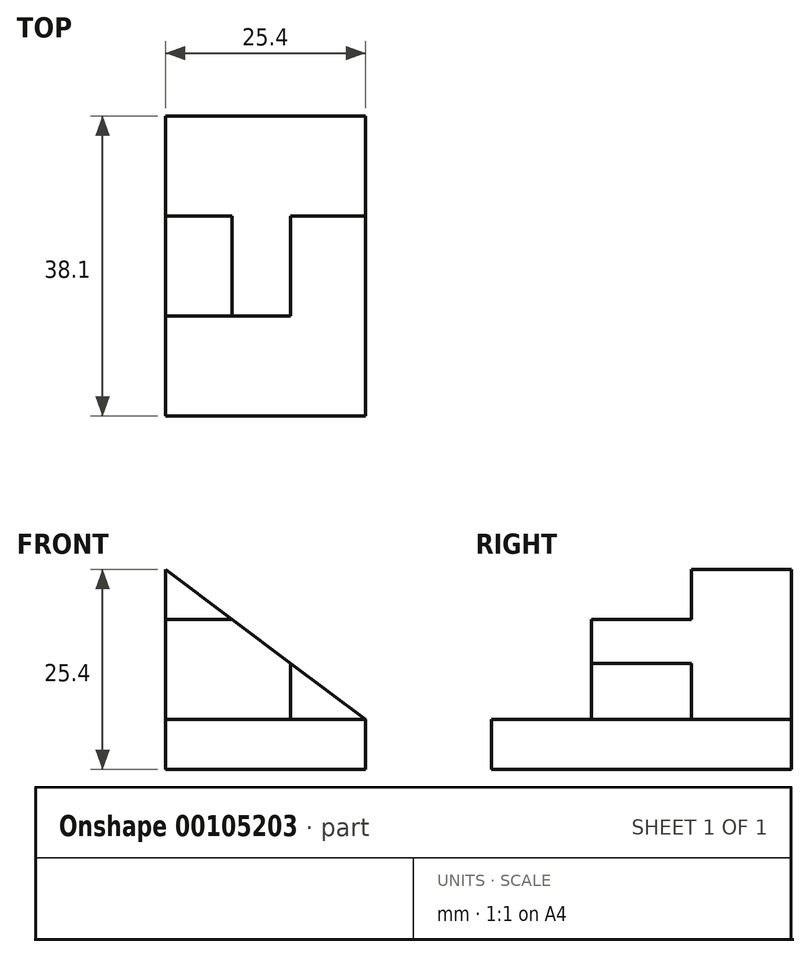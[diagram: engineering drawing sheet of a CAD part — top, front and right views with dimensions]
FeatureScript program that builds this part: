
annotation { "Feature Type Name" : "Feature", "Feature Type Description" : "" }
export const myFeature = defineFeature(function(context is Context, id is Id, definition is map)
    precondition{}
    {
        {
            var Q0;
            Q0=qCreatedBy(makeId("Front.planeOp"),FACE);
            var sketch = newSketch(context, id + "F0", { "sketchPlane" : qUnion([Q0])});
            skLineSegment(sketch, "E0.bottom", {"start": v(0, 0) * mm, "end": v(-25.4, 0) * mm});
            skLineSegment(sketch, "E0.left", {"start": v(0, 0) * mm, "end": v(0, 6.35) * mm});
            skLineSegment(sketch, "E0.right", {"start": v(-25.4, 0) * mm, "end": v(-25.4, 25.4) * mm});
            skLineSegment(sketch, "E1", {"start": v(-25.4, 25.4) * mm, "end": v(0, 6.35) * mm});
            skSolve(sketch);
        }
        {
            var Q0;
            Q0 = qSketchRegion(id + "F0", true);
            extrude(context, id + "F1", {"entities" : qUnion([Q0]), "oppositeDirection" : true, "depth" : 38.1 * mm});
        }
        {
            var Q0;
            Q0=qCreatedBy(makeId("Right.planeOp"),FACE);
            var sketch = newSketch(context, id + "F2", { "sketchPlane" : qUnion([Q0])});
            skLineSegment(sketch, "E2.bottom", {"start": v(12.7, 25.4) * mm, "end": v(0, 25.4) * mm});
            skLineSegment(sketch, "E2.top", {"start": v(12.7, 6.35) * mm, "end": v(0, 6.35) * mm});
            skLineSegment(sketch, "E2.left", {"start": v(12.7, 25.4) * mm, "end": v(12.7, 6.35) * mm});
            skLineSegment(sketch, "E2.right", {"start": v(0, 25.4) * mm, "end": v(0, 6.35) * mm});
            skSolve(sketch);
        }
        {
            var Q0;
            Q0 = qSketchRegion(id + "F2", true);
            extrude(context, id + "F3", {"entities" : qUnion([Q0]), "operationType" : NewBodyOperationType.REMOVE, "oppositeDirection" : true, "depth" : 25.4 * mm});
        }
        {
            var Q0;
            Q0=qCreatedBy(makeId("Right.planeOp"),FACE);
            var sketch = newSketch(context, id + "F4", { "sketchPlane" : qUnion([Q0])});
            skLineSegment(sketch, "E3.bottom", {"start": v(12.7, 25.4) * mm, "end": v(25.4, 25.4) * mm});
            skLineSegment(sketch, "E3.top", {"start": v(12.7, 19.05) * mm, "end": v(25.4, 19.05) * mm});
            skLineSegment(sketch, "E3.left", {"start": v(12.7, 25.4) * mm, "end": v(12.7, 19.05) * mm});
            skLineSegment(sketch, "E3.right", {"start": v(25.4, 25.4) * mm, "end": v(25.4, 19.05) * mm});
            skSolve(sketch);
        }
        {
            var Q0;
            Q0 = qSketchRegion(id + "F4", true);
            extrude(context, id + "F5", {"entities" : qUnion([Q0]), "operationType" : NewBodyOperationType.REMOVE, "oppositeDirection" : true, "depth" : 25.4 * mm});
        }
        {
            var Q0;
            Q0=qCreatedBy(makeId("Front.planeOp"),FACE);
            var sketch = newSketch(context, id + "F6", { "sketchPlane" : qUnion([Q0])});
            skLineSegment(sketch, "E4", {"start": v(-9.53, 13.5) * mm, "end": v(-9.53, 6.35) * mm});
            skLineSegment(sketch, "E5", {"start": v(-9.53, 6.35) * mm, "end": v(0, 6.35) * mm});
            skLineSegment(sketch, "E6", {"start": v(0, 6.35) * mm, "end": v(-9.53, 13.5) * mm});
            skSolve(sketch);
        }
        {
            var Q0;
            Q0 = qSketchRegion(id + "F6", true);
            extrude(context, id + "F7", {"entities" : qUnion([Q0]), "operationType" : NewBodyOperationType.REMOVE, "oppositeDirection" : true, "depth" : 25.4 * mm});
        }
    });
